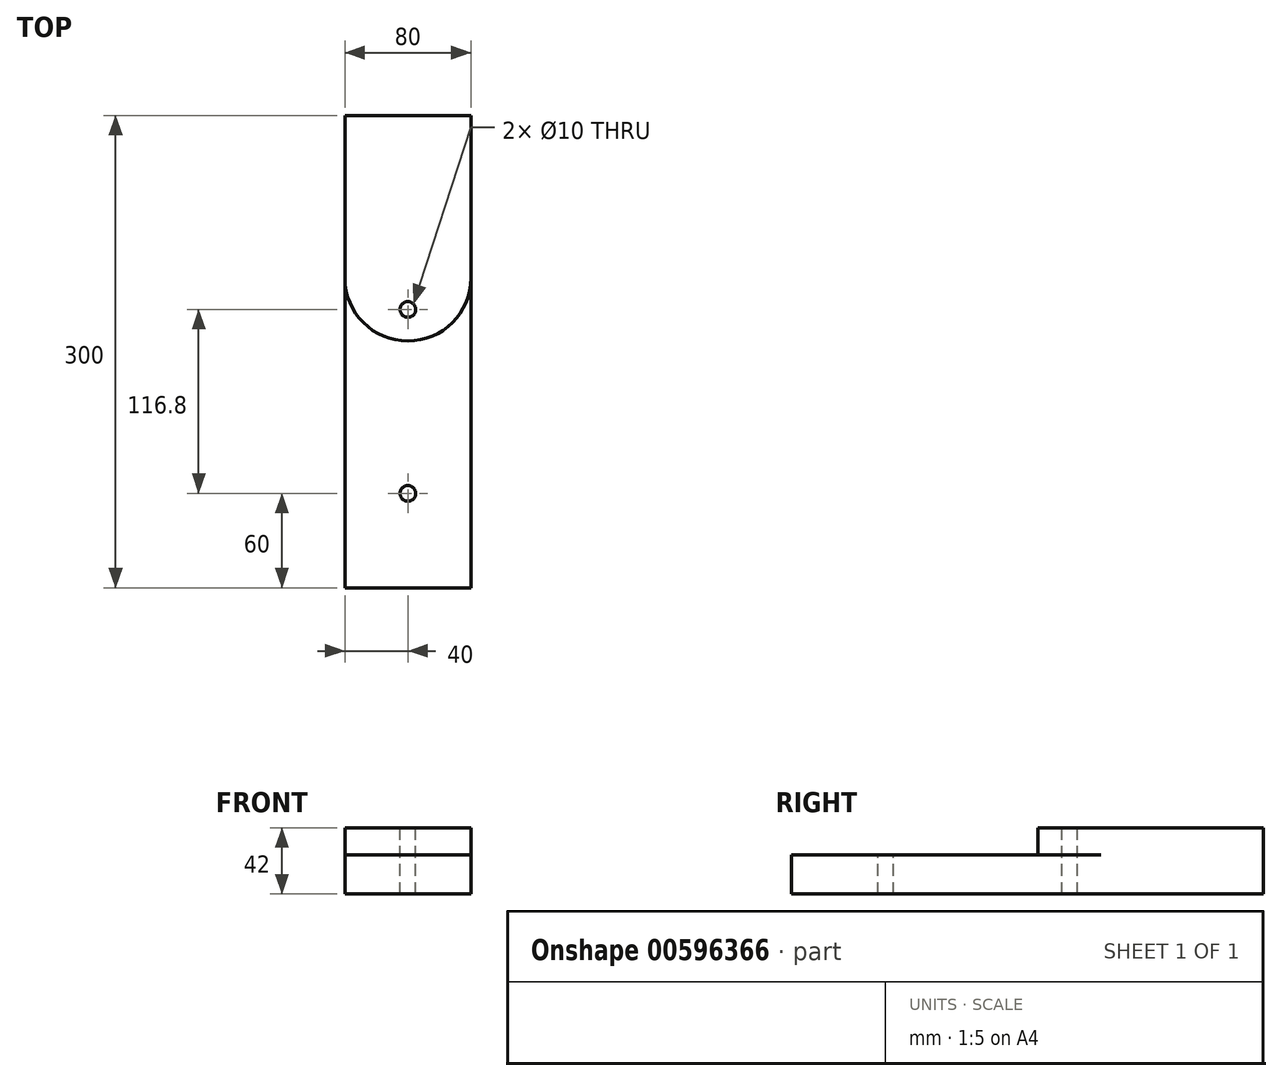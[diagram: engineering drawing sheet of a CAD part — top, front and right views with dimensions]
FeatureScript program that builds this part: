
annotation { "Feature Type Name" : "Feature", "Feature Type Description" : "" }
export const myFeature = defineFeature(function(context is Context, id is Id, definition is map)
    precondition{}
    {
        {
            var Q0;
            Q0=qCreatedBy(makeId("Top.planeOp"),FACE);
            var sketch = newSketch(context, id + "F0", { "sketchPlane" : qUnion([Q0])});
            skLineSegment(sketch, "E0.bottom", {"start": v(40, -150) * mm, "end": v(-40, -150) * mm});
            skLineSegment(sketch, "E0.top", {"start": v(40, 150) * mm, "end": v(-40, 150) * mm});
            skLineSegment(sketch, "E0.left", {"start": v(40, -150) * mm, "end": v(40, 150) * mm});
            skLineSegment(sketch, "E0.right", {"start": v(-40, -150) * mm, "end": v(-40, 150) * mm});
            skPoint(sketch, "E0.middle", {"position": v(0, 0) * mm});
            skCircle(sketch, "E1", {"center": v(0, 26.8) * mm, "radius": 5 * mm});
            skCircle(sketch, "E2", {"center": v(0, -90) * mm, "radius": 5 * mm});
            skLineSegment(sketch, "E3", {"start": v(-51.98, 46.8) * mm, "end": v(60.51, 46.8) * mm, "construction": true});
            skArc(sketch, "E4", {"start": v(-40, 46.8) * mm, "mid": v(0, 6.73) * mm, "end": v(40, 46.8) * mm});
            skSolve(sketch);
        }
        {
            var Q0;
            {var subQ1=sQuery(id+"F0.wireOp",EDGE,"E0.bottom");Q0=makeQuery(id+"F0.imprint","IMPRINT",FACE,{"disambiguationData":[TD([[makeQuery(id+"F0.imprint","IMPRINT",EDGE,{"derivedFrom":subQ1}),-1.0]])]});}
            var Q1;
            {var subQ1=sQuery(id+"F0.wireOp",EDGE,"E0.top");Q1=makeQuery(id+"F0.imprint","IMPRINT",FACE,{"disambiguationData":[TD([[makeQuery(id+"F0.imprint","IMPRINT",EDGE,{"derivedFrom":subQ1}),1.0]])]});}
            extrude(context, id + "F1", {"entities" : qUnion([Q0, Q1]), "oppositeDirection" : true, "depth" : 25 * mm, "offsetDistance" : 25 * mm});
        }
        {
            var Q0;
            {var subQ1=sQuery(id+"F0.wireOp",EDGE,"E0.top");Q0=makeQuery(id+"F0.imprint","IMPRINT",FACE,{"disambiguationData":[TD([[makeQuery(id+"F0.imprint","IMPRINT",EDGE,{"derivedFrom":subQ1}),1.0]])]});}
            extrude(context, id + "F2", {"entities" : qUnion([Q0]), "operationType" : NewBodyOperationType.ADD, "depth" : 17 * mm, "offsetDistance" : 25 * mm});
        }
    });
